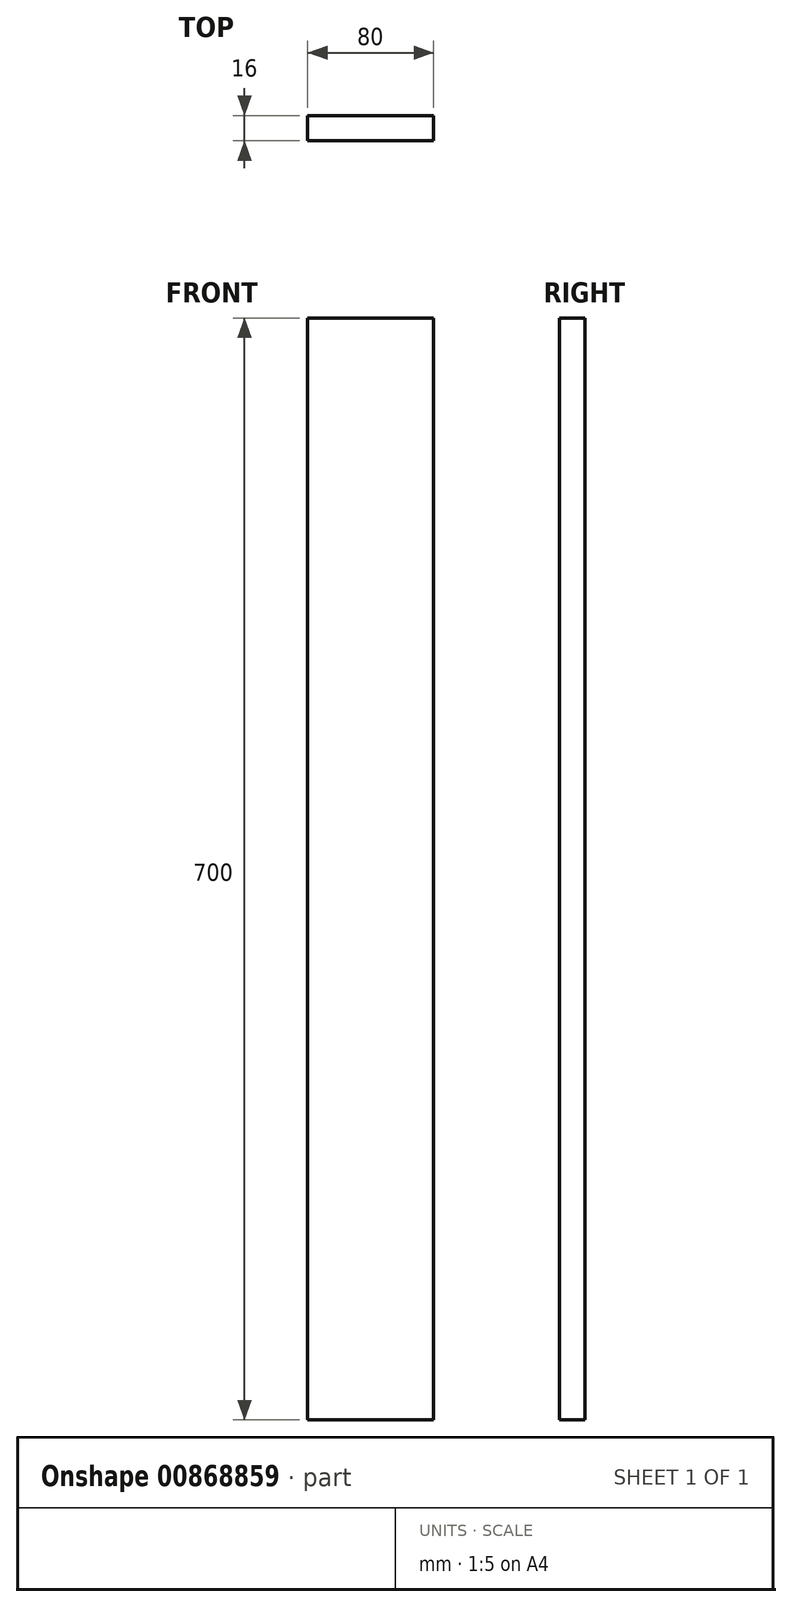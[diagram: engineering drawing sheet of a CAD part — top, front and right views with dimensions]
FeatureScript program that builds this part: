
annotation { "Feature Type Name" : "Feature", "Feature Type Description" : "" }
export const myFeature = defineFeature(function(context is Context, id is Id, definition is map)
    precondition{}
    {
        {
            var Q0;
            Q0=qCreatedBy(makeId("Front.planeOp"),FACE);
            var sketch = newSketch(context, id + "F0", { "sketchPlane" : qUnion([Q0])});
            skLineSegment(sketch, "E0.bottom", {"start": v(0, 0) * mm, "end": v(80, 0) * mm});
            skLineSegment(sketch, "E0.top", {"start": v(0, 700) * mm, "end": v(80, 700) * mm});
            skLineSegment(sketch, "E0.left", {"start": v(0, 0) * mm, "end": v(0, 700) * mm});
            skLineSegment(sketch, "E0.right", {"start": v(80, 0) * mm, "end": v(80, 700) * mm});
            skSolve(sketch);
        }
        {
            var Q0;
            Q0=makeQuery(id+"F0.imprint","IMPRINT",FACE,{"disambiguationData":[TD([[makeQuery(id+"F0.imprint","IMPRINT",EDGE,{"derivedFrom":sQuery(id+"F0.wireOp",EDGE,"E0.bottom")}),1.0]])]});
            extrude(context, id + "F1", {"entities" : qUnion([Q0]), "depth" : 16 * mm, "offsetDistance" : 25 * mm});
        }
    });
